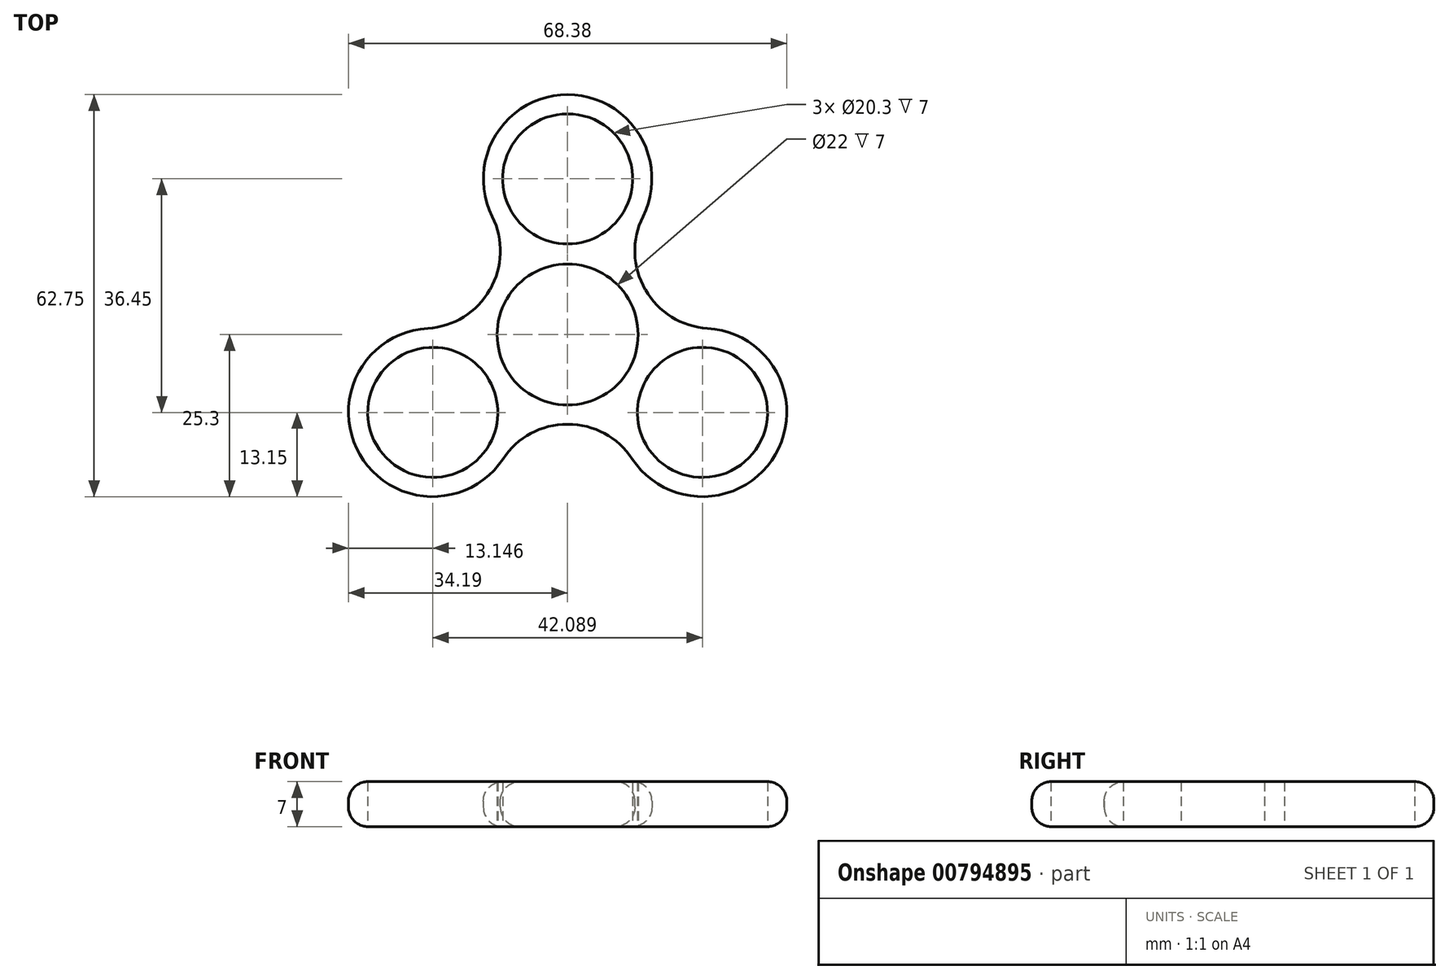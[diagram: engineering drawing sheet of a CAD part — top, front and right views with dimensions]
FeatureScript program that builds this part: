
annotation { "Feature Type Name" : "Feature", "Feature Type Description" : "" }
export const myFeature = defineFeature(function(context is Context, id is Id, definition is map)
    precondition{}
    {
        {
            var Q0;
            Q0=qCreatedBy(makeId("Top.planeOp"),FACE);
            var sketch = newSketch(context, id + "F0", { "sketchPlane" : qUnion([Q0])});
            skCircle(sketch, "E0", {"center": v(0, 0) * mm, "radius": 11 * mm});
            skCircle(sketch, "E1", {"center": v(0, 24.3) * mm, "radius": 10.15 * mm});
            skCircle(sketch, "E2", {"center": v(0, 24.3) * mm, "radius": 13.15 * mm});
            skCircle(sketch, "E3", {"center": v(0, 0) * mm, "radius": 14 * mm});
            skCircle(sketch, "E4.1.0", {"center": v(-21.04, -12.15) * mm, "radius": 10.15 * mm});
            skCircle(sketch, "E4.1.1", {"center": v(-21.04, -12.15) * mm, "radius": 13.15 * mm});
            skCircle(sketch, "E4.2.0", {"center": v(21.04, -12.15) * mm, "radius": 10.15 * mm});
            skCircle(sketch, "E4.2.1", {"center": v(21.04, -12.15) * mm, "radius": 13.15 * mm});
            skSolve(sketch);
        }
        {
            var Q0;
            Q0=qSketchRegion(id+"F0",true);
            var Q1;
            {var subQ0=sQuery(id+"F0.wireOp",EDGE,"6c814f78-6a8c-4767-bfe4-020fc6749d21.1.0");Q1=makeQuery(id+"F0.imprint","IMPRINT",FACE,{"disambiguationData":[TD([[makeQuery(id+"F0.imprint","IMPRINT",EDGE,{"derivedFrom":subQ0}),1.0]])]});}
            var Q2;
            {var subQ0=sQuery(id+"F0.wireOp",EDGE,"6c814f78-6a8c-4767-bfe4-020fc6749d21.2.0");Q2=makeQuery(id+"F0.imprint","IMPRINT",FACE,{"disambiguationData":[TD([[makeQuery(id+"F0.imprint","IMPRINT",EDGE,{"derivedFrom":subQ0}),1.0]])]});}
            var Q3;
            {var subQ0=sQuery(id+"F0.wireOp",EDGE,"uKlYDf5V-o6mg-XEKM-8biU-BISoe1gVwQLA");Q3=makeQuery(id+"F0.imprint","IMPRINT",FACE,{"disambiguationData":[TD([[makeQuery(id+"F0.imprint","IMPRINT",EDGE,{"derivedFrom":subQ0}),1.0]])]});}
            extrude(context, id + "F1", {"entities" : qUnion([Q0, Q1, Q2, Q3]), "endBound" : BoundingType.SYMMETRIC, "depth" : 7 * mm, "offsetDistance" : 25 * mm});
        }
        {
            var Q0;
            {var subQ0=sQuery(id+"F0.wireOp",EDGE,"E3");var subQ1=sQuery(id+"F0.wireOp",EDGE,"E2");Q0=makeQuery(id+"F1.opExtrude","SWEPT_EDGE",EDGE,{"disambiguationData":[OSD([subQ1,subQ0]),TDD([makeQuery(id+"F0.imprint","INTERSECT",VERTEX,{"disambiguationData":[OD(0.0)],"derivedFrom":[subQ1,subQ0]})])]});}
            var Q1;
            {var subQ0=sQuery(id+"F0.wireOp",EDGE,"E4.1.1");var subQ1=sQuery(id+"F0.wireOp",EDGE,"E3");Q1=makeQuery(id+"F1.opExtrude","SWEPT_EDGE",EDGE,{"disambiguationData":[OSD([subQ1,subQ0]),TDD([makeQuery(id+"F0.imprint","INTERSECT",VERTEX,{"disambiguationData":[OD(0.0)],"derivedFrom":[subQ1,subQ0]})])]});}
            var Q2;
            {var subQ0=sQuery(id+"F0.wireOp",EDGE,"E3");var subQ1=sQuery(id+"F0.wireOp",EDGE,"E2");Q2=makeQuery(id+"F1.opExtrude","SWEPT_EDGE",EDGE,{"disambiguationData":[OSD([subQ1,subQ0]),TDD([makeQuery(id+"F0.imprint","INTERSECT",VERTEX,{"disambiguationData":[OD(1.0)],"derivedFrom":[subQ1,subQ0]})])]});}
            var Q3;
            {var subQ0=sQuery(id+"F0.wireOp",EDGE,"E4.2.1");var subQ1=sQuery(id+"F0.wireOp",EDGE,"E3");Q3=makeQuery(id+"F1.opExtrude","SWEPT_EDGE",EDGE,{"disambiguationData":[OSD([subQ1,subQ0]),TDD([makeQuery(id+"F0.imprint","INTERSECT",VERTEX,{"disambiguationData":[OD(1.0)],"derivedFrom":[subQ1,subQ0]})])]});}
            var Q4;
            {var subQ0=sQuery(id+"F0.wireOp",EDGE,"E4.2.1");var subQ1=sQuery(id+"F0.wireOp",EDGE,"E3");Q4=makeQuery(id+"F1.opExtrude","SWEPT_EDGE",EDGE,{"disambiguationData":[OSD([subQ1,subQ0]),TDD([makeQuery(id+"F0.imprint","INTERSECT",VERTEX,{"disambiguationData":[OD(0.0)],"derivedFrom":[subQ1,subQ0]})])]});}
            var Q5;
            {var subQ0=sQuery(id+"F0.wireOp",EDGE,"E4.1.1");var subQ1=sQuery(id+"F0.wireOp",EDGE,"E3");Q5=makeQuery(id+"F1.opExtrude","SWEPT_EDGE",EDGE,{"disambiguationData":[OSD([subQ1,subQ0]),TDD([makeQuery(id+"F0.imprint","INTERSECT",VERTEX,{"disambiguationData":[OD(1.0)],"derivedFrom":[subQ1,subQ0]})])]});}
            fillet(context, id + "F2", {"entities" : qUnion([Q0, Q1, Q2, Q3, Q4, Q5]), "radius" : 12 * mm, "tangentPropagation" : true, "allowEdgeOverflow" : false});
        }
        {
            var Q0;
            Q0=makeQuery(id+"F1.opExtrude","CAP_EDGE",EDGE,{"disambiguationData":[OSD([sQuery(id+"F0.wireOp",EDGE,"E4.2.1")])],"isStart":true});
            var Q1;
            Q1=makeQuery(id+"F1.opExtrude","CAP_EDGE",EDGE,{"disambiguationData":[OSD([sQuery(id+"F0.wireOp",EDGE,"E4.1.1")])],"isStart":true});
            var Q2;
            Q2=makeQuery(id+"F1.opExtrude","CAP_EDGE",EDGE,{"disambiguationData":[OSD([sQuery(id+"F0.wireOp",EDGE,"E2")])],"isStart":true});
            var Q3;
            Q3=makeQuery(id+"F1.opExtrude","CAP_EDGE",EDGE,{"disambiguationData":[OSD([sQuery(id+"F0.wireOp",EDGE,"E4.1.1")])],"isStart":false});
            var Q4;
            Q4=makeQuery(id+"F1.opExtrude","CAP_EDGE",EDGE,{"disambiguationData":[OSD([sQuery(id+"F0.wireOp",EDGE,"E2")])],"isStart":false});
            var Q5;
            Q5=makeQuery(id+"F1.opExtrude","CAP_EDGE",EDGE,{"disambiguationData":[OSD([sQuery(id+"F0.wireOp",EDGE,"E4.2.1")])],"isStart":false});
            fillet(context, id + "F3", {"entities" : qUnion([Q0, Q1, Q2, Q3, Q4, Q5]), "radius" : 3 * mm, "tangentPropagation" : true, "allowEdgeOverflow" : false});
        }
    });
